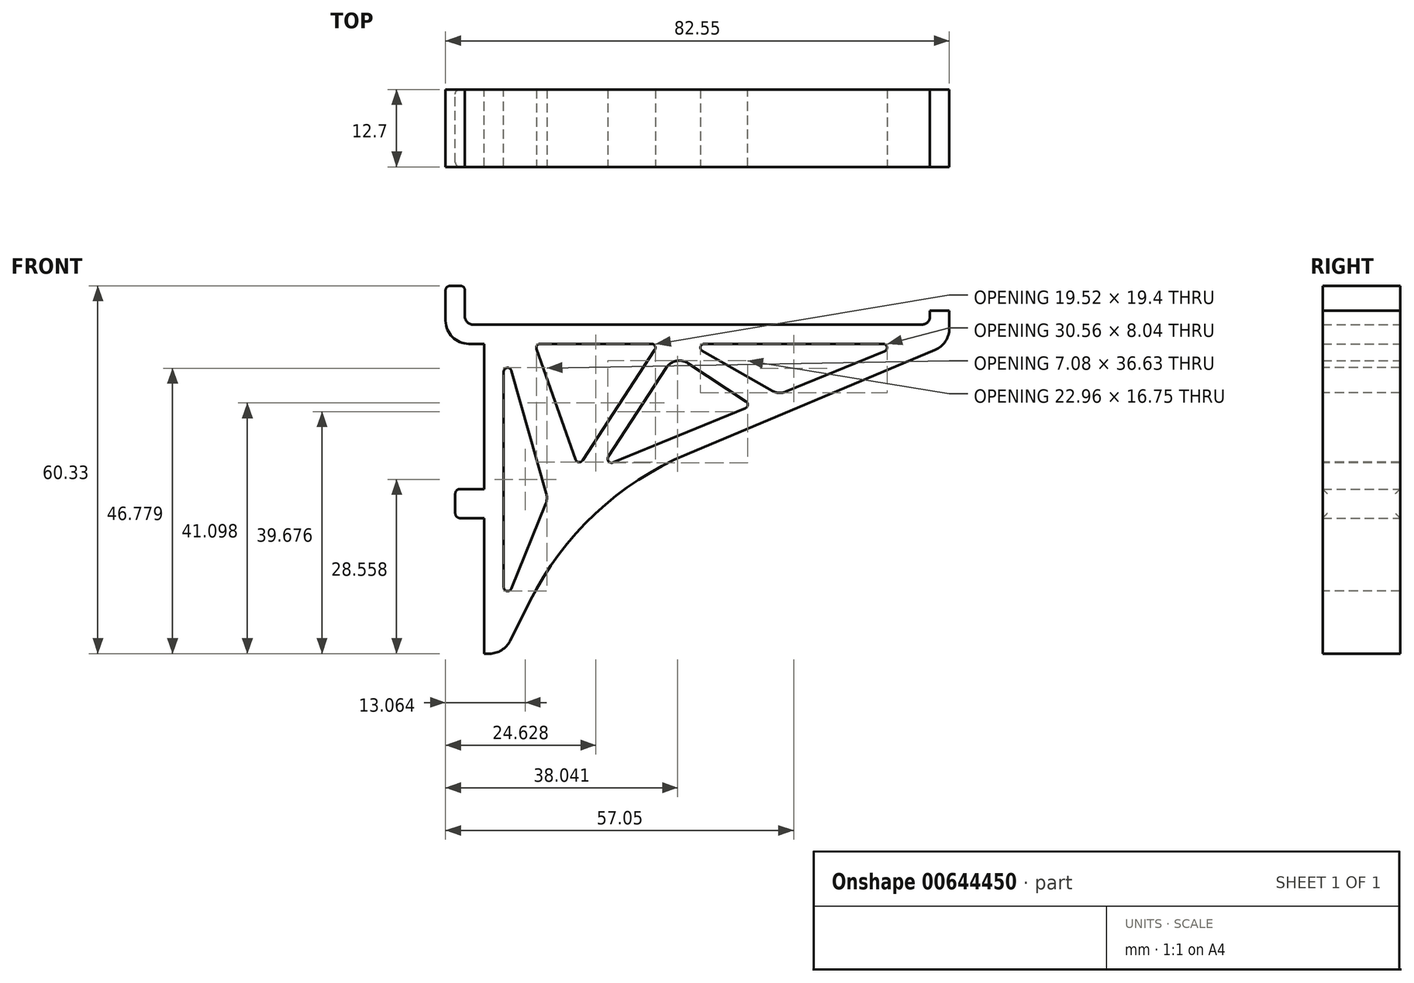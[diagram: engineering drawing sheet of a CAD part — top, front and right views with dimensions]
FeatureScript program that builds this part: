
annotation { "Feature Type Name" : "Feature", "Feature Type Description" : "" }
export const myFeature = defineFeature(function(context is Context, id is Id, definition is map)
    precondition{}
    {
        {
            var Q0;
            Q0=qCreatedBy(makeId("Front.planeOp"),FACE);
            var sketch = newSketch(context, id + "F0", { "sketchPlane" : qUnion([Q0])});
            skLineSegment(sketch, "E0.left", {"start": v(0, 9.52) * mm, "end": v(0, 0) * mm});
            skLineSegment(sketch, "E0.right", {"start": v(82.55, 9.52) * mm, "end": v(82.55, 0) * mm});
            skLineSegment(sketch, "E1.bottom", {"start": v(3.17, 9.52) * mm, "end": v(79.38, 9.52) * mm, "construction": true});
            skLineSegment(sketch, "E1.top", {"start": v(3.18, 3.17) * mm, "end": v(79.38, 3.17) * mm});
            skLineSegment(sketch, "E1.left", {"start": v(3.17, 9.52) * mm, "end": v(3.17, 3.17) * mm});
            skLineSegment(sketch, "E1.right", {"start": v(79.38, 9.52) * mm, "end": v(79.38, 3.17) * mm});
            skLineSegment(sketch, "E2.top", {"start": v(3.18, -50.8) * mm, "end": v(82.55, -50.8) * mm});
            skLineSegment(sketch, "E2.left", {"start": v(3.17, 0) * mm, "end": v(3.18, -50.8) * mm, "construction": true});
            skLineSegment(sketch, "E2.right", {"start": v(82.55, 0) * mm, "end": v(82.55, -50.8) * mm});
            skLineSegment(sketch, "E3", {"start": v(6.35, 0) * mm, "end": v(6.35, -50.8) * mm});
            skLineSegment(sketch, "E4", {"start": v(79.38, 5.45) * mm, "end": v(82.55, 5.45) * mm});
            skLineSegment(sketch, "E5", {"start": v(0, 9.52) * mm, "end": v(3.17, 9.52) * mm});
            skLineSegment(sketch, "E6", {"start": v(0, 0) * mm, "end": v(6.35, 0) * mm});
            skLineSegment(sketch, "E7", {"start": v(22.23, 3.18) * mm, "end": v(22.23, -50.8) * mm, "construction": true});
            skLineSegment(sketch, "E8", {"start": v(6.35, -25.4) * mm, "end": v(82.55, -25.4) * mm, "construction": true});
            skLineSegment(sketch, "E9", {"start": v(9.52, 3.18) * mm, "end": v(9.53, -50.8) * mm, "construction": true});
            skLineSegment(sketch, "E10", {"start": v(9.53, -50.8) * mm, "end": v(22.23, -25.4) * mm});
            skLineSegment(sketch, "E11", {"start": v(22.22, -25.4) * mm, "end": v(82.55, 0) * mm});
            skLineSegment(sketch, "E12.bottom", {"start": v(6.35, -23.81) * mm, "end": v(1.59, -23.81) * mm});
            skLineSegment(sketch, "E12.top", {"start": v(6.35, -28.58) * mm, "end": v(1.59, -28.58) * mm});
            skLineSegment(sketch, "E12.left", {"start": v(6.35, -23.81) * mm, "end": v(6.35, -28.58) * mm});
            skLineSegment(sketch, "E12.right", {"start": v(1.59, -23.81) * mm, "end": v(1.59, -28.58) * mm});
            skLineSegment(sketch, "E13", {"start": v(6.35, 0) * mm, "end": v(82.55, 0) * mm, "construction": true});
            skLineSegment(sketch, "E14", {"start": v(6.35, -21.6) * mm, "end": v(82.55, -21.6) * mm, "construction": true});
            skLineSegment(sketch, "E15", {"start": v(9.53, 0) * mm, "end": v(9.53, -43.18) * mm});
            skLineSegment(sketch, "E16", {"start": v(16.75, 3.17) * mm, "end": v(16.75, -50.8) * mm, "construction": true});
            skLineSegment(sketch, "E17", {"start": v(9.53, -43.18) * mm, "end": v(16.75, -25.4) * mm});
            skLineSegment(sketch, "E18", {"start": v(16.75, -25.4) * mm, "end": v(9.53, 0) * mm});
            skLineSegment(sketch, "E19", {"start": v(14.6, 3.18) * mm, "end": v(14.6, -50.8) * mm, "construction": true});
            skLineSegment(sketch, "E20", {"start": v(74.93, 3.17) * mm, "end": v(74.93, -50.8) * mm, "construction": true});
            skLineSegment(sketch, "E21", {"start": v(14.6, 0) * mm, "end": v(22.23, -21.6) * mm, "construction": true});
            skLineSegment(sketch, "E22", {"start": v(22.23, -21.6) * mm, "end": v(74.93, 0) * mm, "construction": true});
            skLineSegment(sketch, "E23", {"start": v(74.93, 0) * mm, "end": v(14.6, 0) * mm});
            skLineSegment(sketch, "E24", {"start": v(34.93, 3.18) * mm, "end": v(34.93, -50.8) * mm, "construction": true});
            skLineSegment(sketch, "E25", {"start": v(38.74, 3.18) * mm, "end": v(38.74, -50.8) * mm, "construction": true});
            skLineSegment(sketch, "E26", {"start": v(34.93, 0) * mm, "end": v(21.73, -20.2) * mm, "construction": true});
            skLineSegment(sketch, "E27", {"start": v(38.74, 0) * mm, "end": v(25.55, -20.23) * mm, "construction": true});
            skLineSegment(sketch, "E28", {"start": v(14.6, 0) * mm, "end": v(21.73, -20.2) * mm});
            skLineSegment(sketch, "E29", {"start": v(21.73, -20.2) * mm, "end": v(34.93, 0) * mm});
            skLineSegment(sketch, "E30", {"start": v(25.55, -20.23) * mm, "end": v(74.93, 0) * mm});
            skLineSegment(sketch, "E31", {"start": v(51.44, 3.18) * mm, "end": v(51.44, -50.8) * mm, "construction": true});
            skLineSegment(sketch, "E32", {"start": v(54.61, 3.18) * mm, "end": v(54.61, -50.8) * mm, "construction": true});
            skLineSegment(sketch, "E33", {"start": v(34.93, 0) * mm, "end": v(50.24, -10.11) * mm, "construction": true});
            skLineSegment(sketch, "E34", {"start": v(25.55, -20.23) * mm, "end": v(37.59, -1.76) * mm, "construction": true});
            skLineSegment(sketch, "E35", {"start": v(37.59, -1.76) * mm, "end": v(50.24, -10.11) * mm});
            skLineSegment(sketch, "E36", {"start": v(37.59, -1.76) * mm, "end": v(25.55, -20.23) * mm});
            skLineSegment(sketch, "E37", {"start": v(40, 3.18) * mm, "end": v(40, -50.8) * mm, "construction": true});
            skLineSegment(sketch, "E38", {"start": v(40, 0) * mm, "end": v(54.61, -8.32) * mm});
            skSolve(sketch);
        }
        {
            var Q0;
            Q0=makeQuery(id+"F0.imprint","IMPRINT",FACE,{"disambiguationData":[TD([[makeQuery(id+"F0.imprint","IMPRINT",EDGE,{"derivedFrom":sQuery(id+"F0.wireOp",EDGE,"E0.left")}),1.0]])]});
            var Q1;
            Q1=makeQuery(id+"F0.imprint","IMPRINT",FACE,{"disambiguationData":[TD([[makeQuery(id+"F0.imprint","IMPRINT",EDGE,{"derivedFrom":sQuery(id+"F0.wireOp",EDGE,"E12.bottom")}),1.0]])]});
            extrude(context, id + "F1", {"entities" : qUnion([Q0, Q1]), "depth" : 12.7 * mm, "offsetDistance" : 25.4 * mm});
        }
        {
            var Q0;
            Q0=makeQuery(id+"F1.opExtrude","SWEPT_EDGE",EDGE,{"disambiguationData":[OSD([sQuery(id+"F0.wireOp",EDGE,"E1.top"),sQuery(id+"F0.wireOp",EDGE,"E1.right")])]});
            var Q1;
            Q1=makeQuery(id+"F1.opExtrude","SWEPT_EDGE",EDGE,{"disambiguationData":[OSD([sQuery(id+"F0.wireOp",EDGE,"E1.top"),sQuery(id+"F0.wireOp",EDGE,"E1.left")])]});
            fillet(context, id + "F2", {"entities" : qUnion([Q0, Q1]), "radius" : 1.27 * mm, "tangentPropagation" : true, "allowEdgeOverflow" : false});
        }
        {
            var Q0;
            Q0=makeQuery(id+"F1.opExtrude","SWEPT_EDGE",EDGE,{"disambiguationData":[OSD([sQuery(id+"F0.wireOp",EDGE,"E0.right"),sQuery(id+"F0.wireOp",EDGE,"E2.right"),sQuery(id+"F0.wireOp",EDGE,"E11")])]});
            var Q1;
            Q1=makeQuery(id+"F1.opExtrude","SWEPT_EDGE",EDGE,{"disambiguationData":[OSD([sQuery(id+"F0.wireOp",EDGE,"E0.left"),sQuery(id+"F0.wireOp",EDGE,"E6")])]});
            var Q2;
            Q2=makeQuery(id+"F1.opExtrude","SWEPT_EDGE",EDGE,{"disambiguationData":[OSD([sQuery(id+"F0.wireOp",EDGE,"E2.top"),sQuery(id+"F0.wireOp",EDGE,"E10")])]});
            fillet(context, id + "F3", {"entities" : qUnion([Q0, Q1, Q2]), "radius" : 3.8 * mm, "tangentPropagation" : true, "allowEdgeOverflow" : false});
        }
        {
            var Q0;
            Q0=makeQuery(id+"F1.opExtrude","SWEPT_EDGE",EDGE,{"disambiguationData":[OSD([sQuery(id+"F0.wireOp",EDGE,"E10"),sQuery(id+"F0.wireOp",EDGE,"E11")])]});
            fillet(context, id + "F4", {"entities" : qUnion([Q0]), "radius" : 50.8 * mm, "tangentPropagation" : true, "allowEdgeOverflow" : false});
        }
        {
            var Q0;
            Q0=makeQuery(id+"F1.opExtrude","SWEPT_EDGE",EDGE,{"disambiguationData":[OSD([sQuery(id+"F0.wireOp",EDGE,"E23"),sQuery(id+"F0.wireOp",EDGE,"E30")])]});
            var Q1;
            Q1=makeQuery(id+"F1.opExtrude","SWEPT_EDGE",EDGE,{"disambiguationData":[OSD([sQuery(id+"F0.wireOp",EDGE,"E30"),sQuery(id+"F0.wireOp",EDGE,"E36")])]});
            var Q2;
            Q2=makeQuery(id+"F1.opExtrude","SWEPT_EDGE",EDGE,{"disambiguationData":[OSD([sQuery(id+"F0.wireOp",EDGE,"E30"),sQuery(id+"F0.wireOp",EDGE,"E35")])]});
            var Q3;
            Q3=makeQuery(id+"F1.opExtrude","SWEPT_EDGE",EDGE,{"disambiguationData":[OSD([sQuery(id+"F0.wireOp",EDGE,"E15"),sQuery(id+"F0.wireOp",EDGE,"E18")])]});
            var Q4;
            Q4=makeQuery(id+"F1.opExtrude","SWEPT_EDGE",EDGE,{"disambiguationData":[OSD([sQuery(id+"F0.wireOp",EDGE,"E15"),sQuery(id+"F0.wireOp",EDGE,"E17")])]});
            var Q5;
            Q5=makeQuery(id+"F1.opExtrude","SWEPT_EDGE",EDGE,{"disambiguationData":[OSD([sQuery(id+"F0.wireOp",EDGE,"E23"),sQuery(id+"F0.wireOp",EDGE,"E28")])]});
            var Q6;
            Q6=makeQuery(id+"F1.opExtrude","SWEPT_EDGE",EDGE,{"disambiguationData":[OSD([sQuery(id+"F0.wireOp",EDGE,"E23"),sQuery(id+"F0.wireOp",EDGE,"E29")])]});
            var Q7;
            Q7=makeQuery(id+"F1.opExtrude","SWEPT_EDGE",EDGE,{"disambiguationData":[OSD([sQuery(id+"F0.wireOp",EDGE,"E23"),sQuery(id+"F0.wireOp",EDGE,"E38")])]});
            var Q8;
            Q8=makeQuery(id+"F1.opExtrude","SWEPT_EDGE",EDGE,{"disambiguationData":[OSD([sQuery(id+"F0.wireOp",EDGE,"E28"),sQuery(id+"F0.wireOp",EDGE,"E29")])]});
            fillet(context, id + "F5", {"entities" : qUnion([Q0, Q1, Q2, Q3, Q4, Q5, Q6, Q7, Q8]), "radius" : 0.64 * mm, "tangentPropagation" : true, "allowEdgeOverflow" : false});
        }
        {
            var Q0;
            Q0=makeQuery(id+"F1.opExtrude","SWEPT_EDGE",EDGE,{"disambiguationData":[OSD([sQuery(id+"F0.wireOp",EDGE,"E17"),sQuery(id+"F0.wireOp",EDGE,"E18")])]});
            var Q1;
            Q1=makeQuery(id+"F1.opExtrude","SWEPT_EDGE",EDGE,{"disambiguationData":[OSD([sQuery(id+"F0.wireOp",EDGE,"E35"),sQuery(id+"F0.wireOp",EDGE,"E36")])]});
            var Q2;
            Q2=makeQuery(id+"F1.opExtrude","SWEPT_EDGE",EDGE,{"disambiguationData":[OSD([sQuery(id+"F0.wireOp",EDGE,"E30"),sQuery(id+"F0.wireOp",EDGE,"E38")])]});
            fillet(context, id + "F6", {"entities" : qUnion([Q0, Q1, Q2]), "radius" : 2.54 * mm, "tangentPropagation" : true, "allowEdgeOverflow" : false});
        }
        {
            var Q0;
            Q0=makeQuery(id+"F1.opExtrude","SWEPT_EDGE",EDGE,{"disambiguationData":[OSD([sQuery(id+"F0.wireOp",EDGE,"E0.left"),sQuery(id+"F0.wireOp",EDGE,"E5")])]});
            var Q1;
            Q1=makeQuery(id+"F1.opExtrude","SWEPT_EDGE",EDGE,{"disambiguationData":[OSD([sQuery(id+"F0.wireOp",EDGE,"E1.left"),sQuery(id+"F0.wireOp",EDGE,"E5")])]});
            var Q2;
            Q2=makeQuery(id+"F1.opExtrude","SWEPT_EDGE",EDGE,{"disambiguationData":[OSD([sQuery(id+"F0.wireOp",EDGE,"E12.bottom"),sQuery(id+"F0.wireOp",EDGE,"E12.right")])]});
            var Q3;
            Q3=makeQuery(id+"F1.opExtrude","SWEPT_EDGE",EDGE,{"disambiguationData":[OSD([sQuery(id+"F0.wireOp",EDGE,"E12.top"),sQuery(id+"F0.wireOp",EDGE,"E12.right")])]});
            var Q4;
            Q4=makeQuery(id+"F1.opExtrude","CAP_EDGE",EDGE,{"disambiguationData":[OSD([sQuery(id+"F0.wireOp",EDGE,"E12.right")])],"isStart":false});
            var Q5;
            Q5=makeQuery(id+"F1.opExtrude","CAP_EDGE",EDGE,{"disambiguationData":[OSD([sQuery(id+"F0.wireOp",EDGE,"E12.right")])],"isStart":true});
            fillet(context, id + "F7", {"entities" : qUnion([Q0, Q1, Q2, Q3, Q4, Q5]), "radius" : 0.76 * mm, "tangentPropagation" : true, "allowEdgeOverflow" : false});
        }
    });
